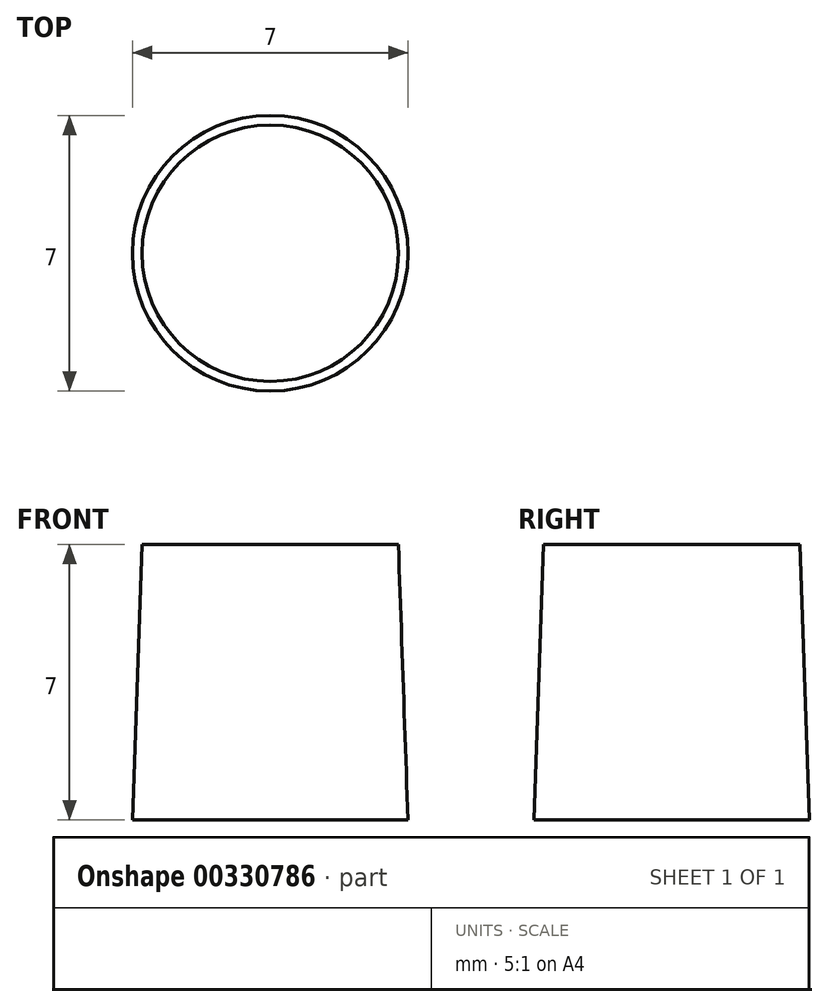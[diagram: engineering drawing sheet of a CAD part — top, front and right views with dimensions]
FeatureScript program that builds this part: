
annotation { "Feature Type Name" : "Feature", "Feature Type Description" : "" }
export const myFeature = defineFeature(function(context is Context, id is Id, definition is map)
    precondition{}
    {
        {
            var Q0;
            Q0=qCreatedBy(makeId("Top.planeOp"),FACE);
            var sketch = newSketch(context, id + "F0", { "sketchPlane" : qUnion([Q0])});
            skCircle(sketch, "E0", {"center": v(0, 0) * mm, "radius": 3.5 * mm});
            skSolve(sketch);
        }
        {
            var Q0;
            Q0 = qSketchRegion(id + "F0", true);
            extrude(context, id + "F1", {"entities" : qUnion([Q0]), "depth" : 7 * mm, "hasDraft" : true, "draftAngle" : 2 * degree, "draftPullDirection" : true});
        }
    });
